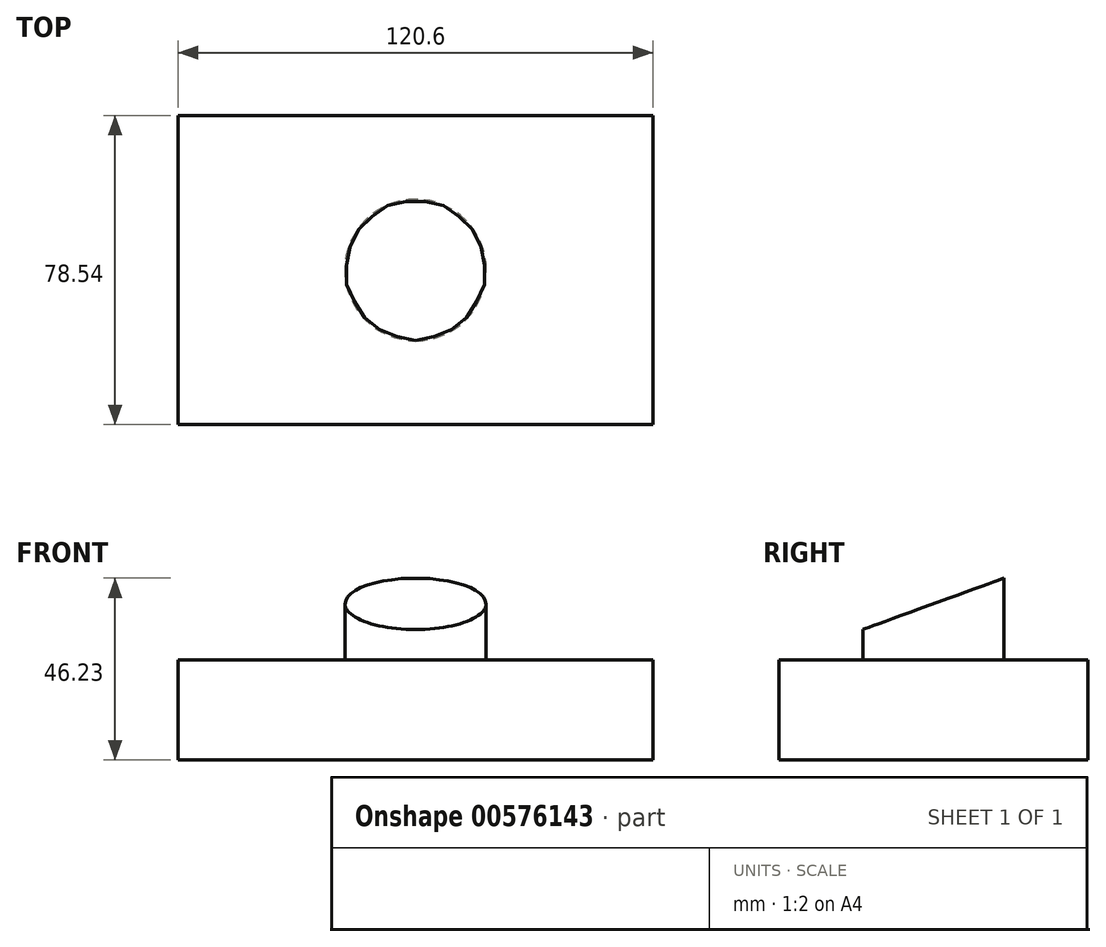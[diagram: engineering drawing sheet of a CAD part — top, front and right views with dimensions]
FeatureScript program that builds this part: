
annotation { "Feature Type Name" : "Feature", "Feature Type Description" : "" }
export const myFeature = defineFeature(function(context is Context, id is Id, definition is map)
    precondition{}
    {
        {
            var Q0;
            Q0=qCreatedBy(makeId("Top.planeOp"),FACE);
            var sketch = newSketch(context, id + "F0", { "sketchPlane" : qUnion([Q0])});
            skLineSegment(sketch, "E0.bottom", {"start": v(-60.3, 39.27) * mm, "end": v(60.3, 39.27) * mm});
            skLineSegment(sketch, "E0.top", {"start": v(-60.3, -39.27) * mm, "end": v(60.3, -39.27) * mm});
            skLineSegment(sketch, "E0.left", {"start": v(-60.3, 39.27) * mm, "end": v(-60.3, -39.27) * mm});
            skLineSegment(sketch, "E0.right", {"start": v(60.3, 39.27) * mm, "end": v(60.3, -39.27) * mm});
            skPoint(sketch, "E0.middle", {"position": v(0, 0) * mm});
            skSolve(sketch);
        }
        {
            var Q0;
            Q0 = qSketchRegion(id + "F0", true);
            extrude(context, id + "F1", {"entities" : qUnion([Q0]), "depth" : 25.4 * mm, "offsetDistance" : 25.4 * mm});
        }
        {
            var Q0;
            Q0=makeQuery(id+"F1.opExtrude","CAP_FACE",FACE,{"disambiguationData":[OSD([sQuery(id+"F0.wireOp",EDGE,"E0.bottom"),sQuery(id+"F0.wireOp",EDGE,"E0.top"),sQuery(id+"F0.wireOp",EDGE,"E0.left"),sQuery(id+"F0.wireOp",EDGE,"E0.right")])],"isStart":false});
            var sketch = newSketch(context, id + "F2", { "sketchPlane" : qUnion([Q0])});
            skCircle(sketch, "E1", {"center": v(0, 0) * mm, "radius": 17.96 * mm});
            skSolve(sketch);
        }
        {
            var Q0;
            Q0=makeQuery(id+"F1.opExtrude","CAP_EDGE",EDGE,{"disambiguationData":[OSD([sQuery(id+"F0.wireOp",EDGE,"E0.top")])],"isStart":false});
            cPlane(context, id + "F3", {"entities" : qUnion([Q0]), "cplaneType" : CPlaneType.LINE_ANGLE, "offset" : 25.4 * mm, "angle" : 70 * degree, "oppositeDirection" : true, "width" : 152.4 * mm, "height" : 152.4 * mm});
        }
        {
            var Q0;
            Q0=makeQuery(id+"F2.imprint","IMPRINT",FACE,{"disambiguationData":[TD([[makeQuery(id+"F2.imprint","IMPRINT",EDGE,{"derivedFrom":sQuery(id+"F2.wireOp",EDGE,"E1")}),1.0]])]});
            var Q1;
            Q1=sQuery(id+"F2.wireOp",EDGE,"E1");
            var Q2;
            Q2=qCreatedBy(id+"F3.planeOp",FACE);
            extrude(context, id + "F4", {"entities" : qUnion([Q0]), "operationType" : NewBodyOperationType.ADD, "surfaceEntities" : qUnion([Q1]), "endBound" : BoundingType.UP_TO_SURFACE, "depth" : 25.4 * mm, "endBoundEntityFace" : qUnion([Q2]), "offsetDistance" : 25.4 * mm});
        }
    });
